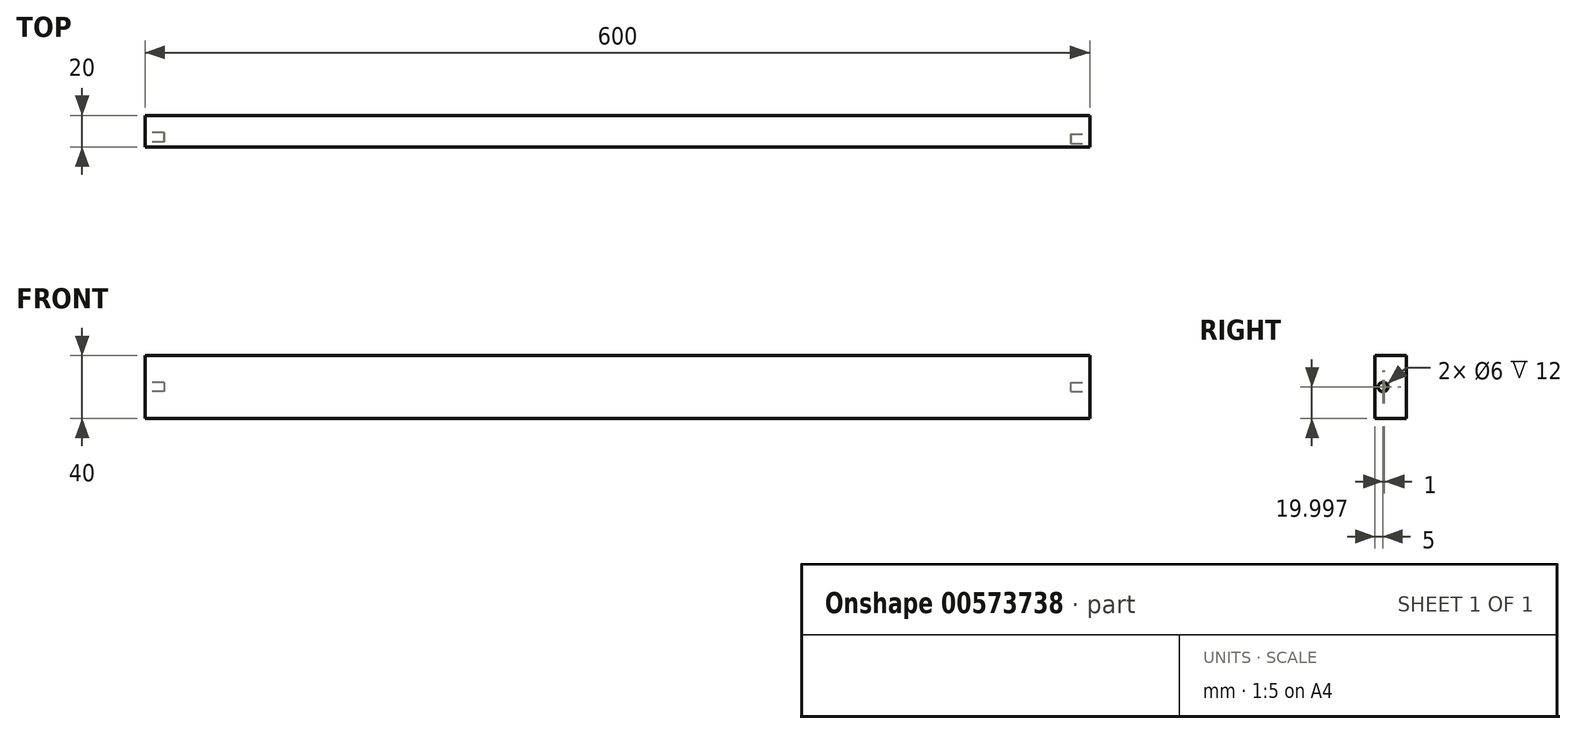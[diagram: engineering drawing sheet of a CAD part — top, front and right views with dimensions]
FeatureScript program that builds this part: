
annotation { "Feature Type Name" : "Feature", "Feature Type Description" : "" }
export const myFeature = defineFeature(function(context is Context, id is Id, definition is map)
    precondition{}
    {
        {
            var Q0;
            Q0=qCreatedBy(makeId("Front.planeOp"),FACE);
            var sketch = newSketch(context, id + "F0", { "sketchPlane" : qUnion([Q0])});
            skLineSegment(sketch, "E0.bottom", {"start": v(-123.29, 79.18) * mm, "end": v(476.71, 79.18) * mm});
            skLineSegment(sketch, "E0.top", {"start": v(-123.29, 39.18) * mm, "end": v(476.71, 39.18) * mm});
            skLineSegment(sketch, "E0.left", {"start": v(-123.29, 79.18) * mm, "end": v(-123.29, 39.18) * mm});
            skLineSegment(sketch, "E0.right", {"start": v(476.71, 79.18) * mm, "end": v(476.71, 39.18) * mm});
            skSolve(sketch);
        }
        {
            var Q0;
            Q0=qSketchRegion(id+"F0",true);
            extrude(context, id + "F1", {"entities" : qUnion([Q0]), "depth" : 20 * mm, "offsetDistance" : 25 * mm});
        }
        {
            var Q0;
            Q0=makeQuery(id+"F1.opExtrude","SWEPT_FACE",FACE,{"disambiguationData":[OSD([sQuery(id+"F0.wireOp",EDGE,"E0.right")])]});
            var sketch = newSketch(context, id + "F2", { "sketchPlane" : qUnion([Q0])});
            skCircle(sketch, "E1", {"center": v(-15, 59.18) * mm, "radius": 3 * mm});
            skSolve(sketch);
        }
        {
            var Q0;
            Q0=makeQuery(id+"F2.imprint","IMPRINT",FACE,{"disambiguationData":[TD([[makeQuery(id+"F2.imprint","IMPRINT",EDGE,{"derivedFrom":sQuery(id+"F2.wireOp",EDGE,"E1")}),1.0]])]});
            extrude(context, id + "F3", {"entities" : qUnion([Q0]), "operationType" : NewBodyOperationType.REMOVE, "oppositeDirection" : true, "depth" : 12 * mm, "offsetDistance" : 25 * mm});
        }
        {
            var Q0;
            Q0=makeQuery(id+"F1.opExtrude","SWEPT_FACE",FACE,{"disambiguationData":[OSD([sQuery(id+"F0.wireOp",EDGE,"E0.left")])]});
            var sketch = newSketch(context, id + "F4", { "sketchPlane" : qUnion([Q0])});
            skCircle(sketch, "E2", {"center": v(14, 59.18) * mm, "radius": 3 * mm});
            skPoint(sketch, "E2.centerSnap0", {"position": v(20, 59.18) * mm});
            skSolve(sketch);
        }
        {
            var Q0;
            Q0=qSketchRegion(id+"F4",true);
            extrude(context, id + "F5", {"entities" : qUnion([Q0]), "operationType" : NewBodyOperationType.REMOVE, "oppositeDirection" : true, "depth" : 12 * mm, "offsetDistance" : 25 * mm});
        }
    });
